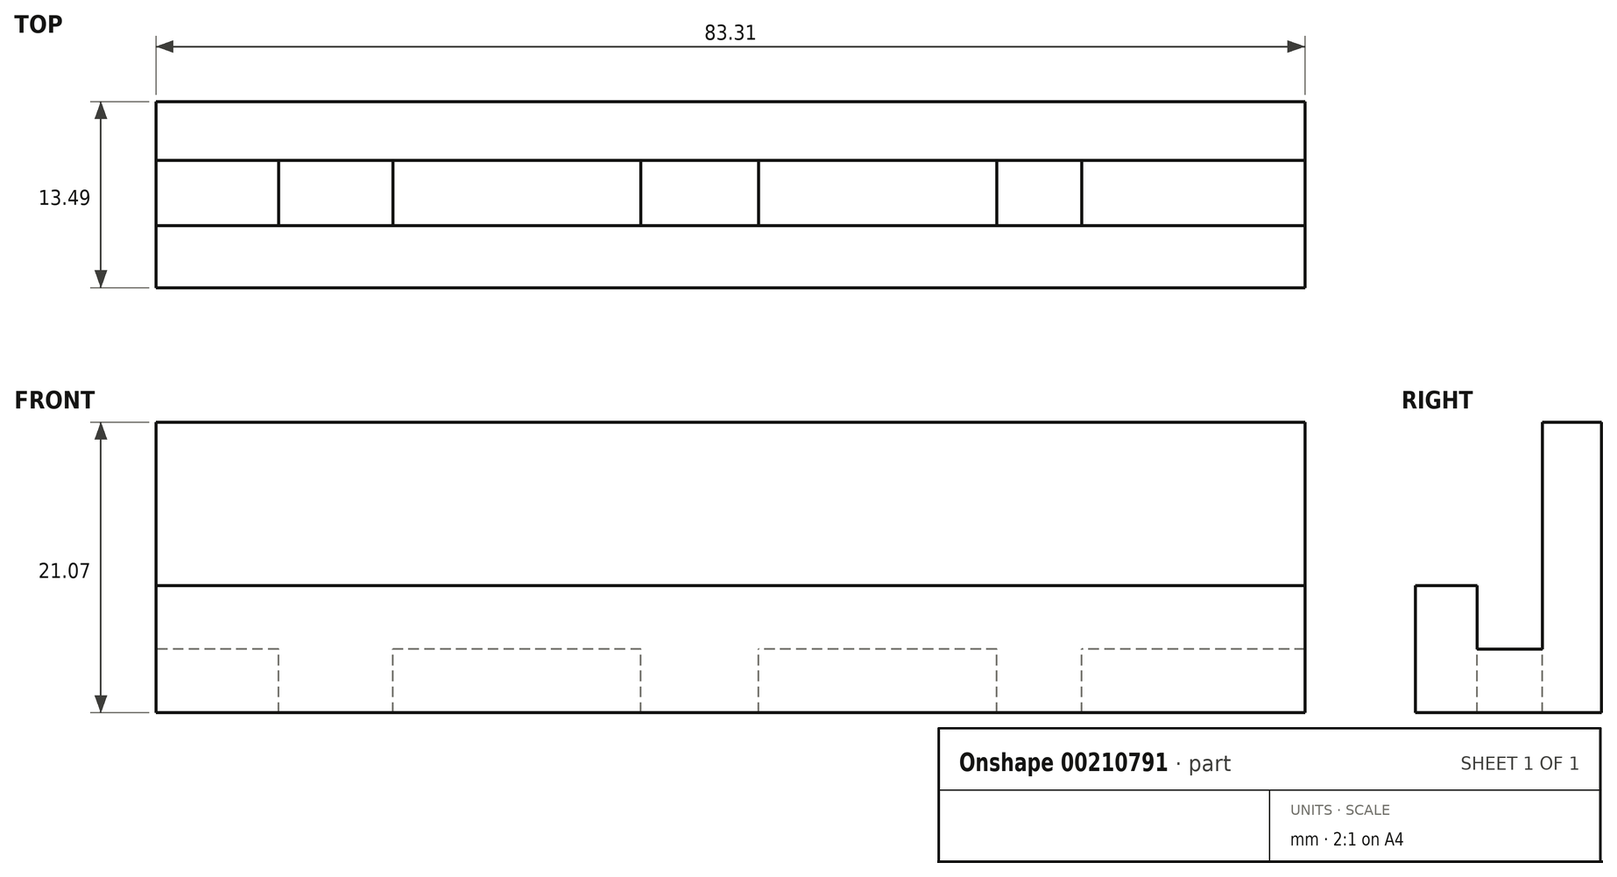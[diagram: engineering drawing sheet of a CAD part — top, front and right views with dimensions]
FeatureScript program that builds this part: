
annotation { "Feature Type Name" : "Feature", "Feature Type Description" : "" }
export const myFeature = defineFeature(function(context is Context, id is Id, definition is map)
    precondition{}
    {
        {
            var Q0;
            Q0=qCreatedBy(makeId("Right.planeOp"),FACE);
            var sketch = newSketch(context, id + "F0", { "sketchPlane" : qUnion([Q0])});
            skLineSegment(sketch, "E0.bottom", {"start": v(-20.12, -9.23) * mm, "end": v(-15.62, -9.23) * mm});
            skLineSegment(sketch, "E0.top", {"start": v(-20.12, 0) * mm, "end": v(-15.62, 0) * mm});
            skLineSegment(sketch, "E0.left", {"start": v(-20.12, -9.23) * mm, "end": v(-20.12, 0) * mm});
            skLineSegment(sketch, "E0.right", {"start": v(-15.62, -9.23) * mm, "end": v(-15.62, 0) * mm});
            skPoint(sketch, "E1.oppositeSnap0", {"position": v(-15.62, -4.62) * mm});
            skLineSegment(sketch, "E1.bottom", {"start": v(-20.12, -9.23) * mm, "end": v(-10.89, -9.23) * mm});
            skLineSegment(sketch, "E1.top", {"start": v(-20.12, -4.62) * mm, "end": v(-10.89, -4.62) * mm});
            skLineSegment(sketch, "E1.left", {"start": v(-20.12, -9.23) * mm, "end": v(-20.12, -4.62) * mm});
            skLineSegment(sketch, "E1.right", {"start": v(-10.89, -9.23) * mm, "end": v(-10.89, -4.62) * mm});
            skLineSegment(sketch, "E2.bottom", {"start": v(-10.89, -9.23) * mm, "end": v(-6.63, -9.23) * mm});
            skLineSegment(sketch, "E2.top", {"start": v(-10.89, 11.84) * mm, "end": v(-6.63, 11.84) * mm});
            skLineSegment(sketch, "E2.left", {"start": v(-10.89, -9.23) * mm, "end": v(-10.89, 11.84) * mm});
            skLineSegment(sketch, "E2.right", {"start": v(-6.63, -9.23) * mm, "end": v(-6.63, 11.84) * mm});
            skSolve(sketch);
        }
        {
            var Q0;
            Q0 = qSketchRegion(id + "F0", true);
            extrude(context, id + "F1", {"entities" : qUnion([Q0]), "depth" : 83.31 * mm});
        }
        {
            var Q0;
            Q0=makeQuery(id+"F1.opExtrude","SWEPT_FACE",FACE,{"disambiguationData":[OSD([sQuery(id+"F0.wireOp",EDGE,"E1.top")])]});
            var sketch = newSketch(context, id + "F2", { "sketchPlane" : qUnion([Q0])});
            skLineSegment(sketch, "E3.bottom", {"start": v(8.88, -10.89) * mm, "end": v(17.17, -10.89) * mm});
            skLineSegment(sketch, "E3.top", {"start": v(8.88, -15.62) * mm, "end": v(17.17, -15.62) * mm});
            skLineSegment(sketch, "E3.left", {"start": v(8.88, -10.89) * mm, "end": v(8.88, -15.62) * mm});
            skLineSegment(sketch, "E3.right", {"start": v(17.17, -10.89) * mm, "end": v(17.17, -15.62) * mm});
            skLineSegment(sketch, "E4.bottom", {"start": v(35.16, -10.89) * mm, "end": v(43.68, -10.89) * mm});
            skLineSegment(sketch, "E4.top", {"start": v(35.16, -15.62) * mm, "end": v(43.68, -15.62) * mm});
            skLineSegment(sketch, "E4.left", {"start": v(35.16, -10.89) * mm, "end": v(35.16, -15.62) * mm});
            skLineSegment(sketch, "E4.right", {"start": v(43.68, -10.89) * mm, "end": v(43.68, -15.62) * mm});
            skLineSegment(sketch, "E5.bottom", {"start": v(60.96, -10.89) * mm, "end": v(67.11, -10.89) * mm});
            skLineSegment(sketch, "E5.top", {"start": v(60.96, -15.62) * mm, "end": v(67.11, -15.62) * mm});
            skLineSegment(sketch, "E5.left", {"start": v(60.96, -10.89) * mm, "end": v(60.96, -15.62) * mm});
            skLineSegment(sketch, "E5.right", {"start": v(67.11, -10.89) * mm, "end": v(67.11, -15.62) * mm});
            skSolve(sketch);
        }
        {
            var Q0;
            Q0 = qSketchRegion(id + "F2", true);
            extrude(context, id + "F3", {"entities" : qUnion([Q0]), "operationType" : NewBodyOperationType.REMOVE, "oppositeDirection" : true, "depth" : 27.94 * mm});
        }
    });
